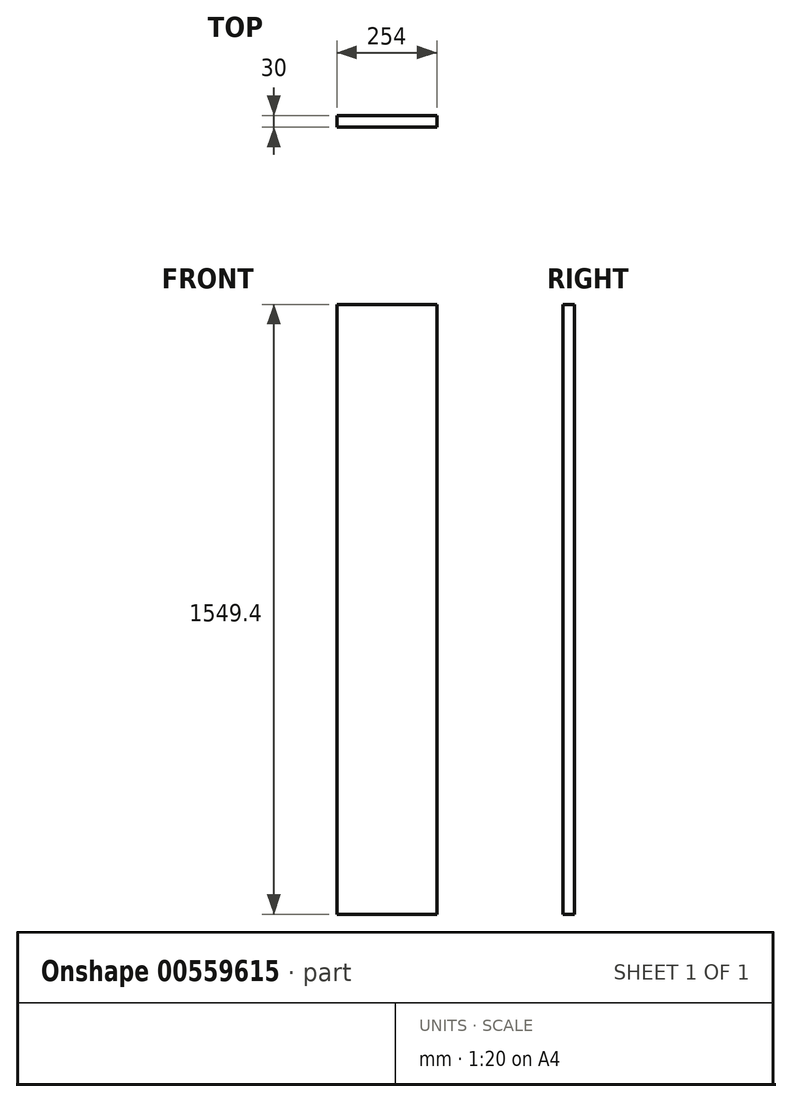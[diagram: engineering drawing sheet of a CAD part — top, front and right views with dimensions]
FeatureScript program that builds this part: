
annotation { "Feature Type Name" : "Feature", "Feature Type Description" : "" }
export const myFeature = defineFeature(function(context is Context, id is Id, definition is map)
    precondition{}
    {
        {
            var Q0;
            Q0=qCreatedBy(makeId("Front.planeOp"),FACE);
            var sketch = newSketch(context, id + "F0", { "sketchPlane" : qUnion([Q0])});
            skLineSegment(sketch, "E0.bottom", {"start": v(127, 774.7) * mm, "end": v(-127, 774.7) * mm});
            skLineSegment(sketch, "E0.top", {"start": v(127, -774.7) * mm, "end": v(-127, -774.7) * mm});
            skLineSegment(sketch, "E0.left", {"start": v(127, 774.7) * mm, "end": v(127, -774.7) * mm});
            skLineSegment(sketch, "E0.right", {"start": v(-127, 774.7) * mm, "end": v(-127, -774.7) * mm});
            skPoint(sketch, "E0.middle", {"position": v(0, 0) * mm});
            skSolve(sketch);
        }
        {
            var Q0;
            Q0 = qSketchRegion(id + "F0", true);
            extrude(context, id + "F1", {"entities" : qUnion([Q0]), "depth" : 30 * mm, "offsetDistance" : 25.4 * mm});
        }
    });
